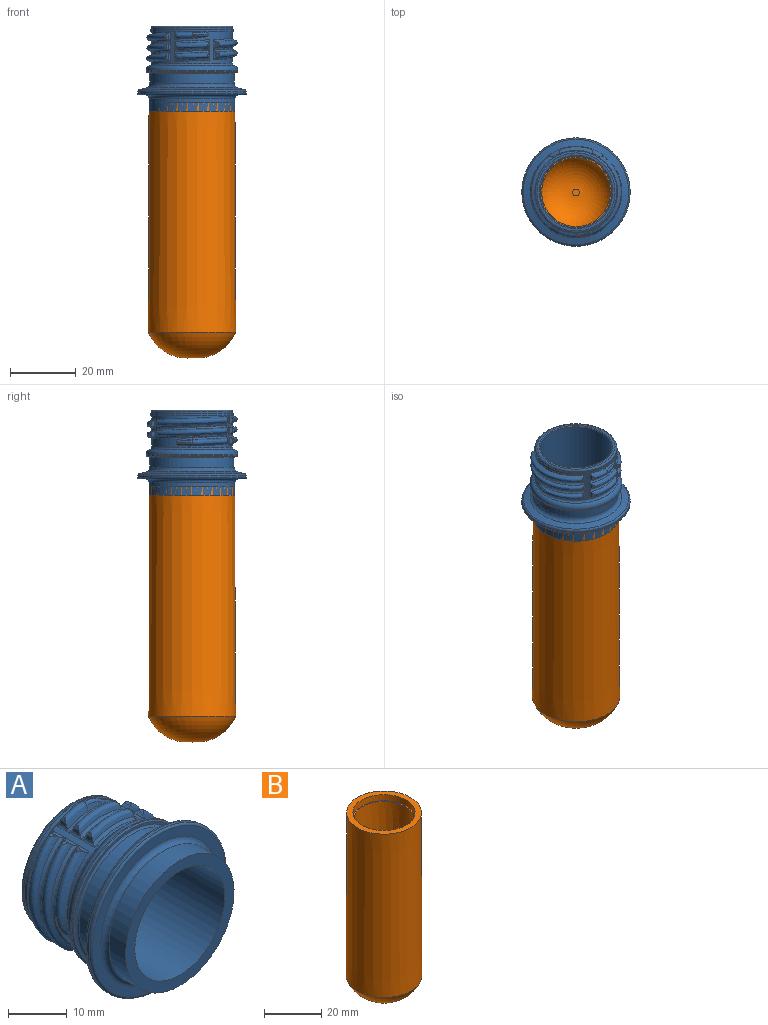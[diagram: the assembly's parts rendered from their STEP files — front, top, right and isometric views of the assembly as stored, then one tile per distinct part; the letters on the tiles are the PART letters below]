
ASSEMBLY  parts=2 mates=1
PART A: 119 faces, bbox 38.3x28.6x38.3 mm
  f0: bspline ~13.4x3.11mm, area 31.2mm2, adj f1,f2,f115,f116,f117,f118
  f1: cylinder r=0.64mm len=1.33mm, axis (0,1,0), area 0mm2, adj f0,f118
  f2: bspline ~12.92x2.26mm, area 8.5mm2, adj f0,f3,f4,f114,f116,f118
  f3: cylinder r=0.58mm len=3mm, axis (0,1,0), area 1.6mm2, adj f2,f4,f116,f117
  f4: cylinder r=12.26mm len=24.51mm, axis (0,-1,0), area 250.7mm2, adj f2,f3,f5,f11,f12,f13,f14,f20
  f5: bspline ~22.44x7.15mm, area 19.3mm2, adj f4,f6,f8,f10,f11,f13
  f6: plane 4.44x3.23mm, normal (-0.53,0,-0.85), area 1.3mm2, adj f5,f7,f8,f11,f12
  f7: cylinder r=0.64mm len=1.34mm, axis (0,1,0), area 0mm2, adj f6,f8
  f8: bspline ~25.39x9.09mm, area 76.1mm2, adj f5,f6,f7,f9,f10,f12
  f9: cylinder r=0.64mm len=1.34mm, axis (0,1,0), area 0mm2, adj f8,f10
  f10: plane 4.44x3.23mm, normal (-0.53,0,0.85), area 1.3mm2, adj f5,f8,f9,f12,f13
  f11: cylinder r=0.58mm len=3mm, axis (0,1,0), area 1.6mm2, adj f4,f5,f6,f12
  f12: bspline ~22.68x7.38mm, area 19.3mm2, adj f4,f6,f8,f10,f11,f13
  f13: cylinder r=0.58mm len=3mm, axis (0,1,0), area 1.6mm2, adj f4,f5,f10,f12
  f14: cylinder r=0.58mm len=3mm, axis (0,1,0), area 1.6mm2, adj f4,f15,f20,f22
  f15: plane 4.44x3.23mm, normal (-0.53,0,-0.85), area 1.3mm2, adj f14,f16,f17,f20,f22
  f16: cylinder r=0.64mm len=1.34mm, axis (0,1,0), area 0mm2, adj f15,f17
  f17: bspline ~25.43x9.14mm, area 75.6mm2, adj f15,f16,f18,f19,f20,f22
  f18: cylinder r=0.64mm len=1.34mm, axis (0,1,0), area 0mm2, adj f17,f19
  f19: plane 4.44x3.23mm, normal (-0.53,0,0.85), area 1.3mm2, adj f17,f18,f20,f21,f22
  f20: bspline ~22.86x7.47mm, area 19.3mm2, adj f4,f14,f15,f17,f19,f21
  f21: cylinder r=0.58mm len=3mm, axis (0,1,0), area 1.6mm2, adj f4,f19,f20,f22
  f22: bspline ~22.44x7.28mm, area 19.3mm2, adj f4,f14,f15,f17,f19,f21
  f23: cylinder r=0.58mm len=2.55mm, axis (0,1,0), area 1.4mm2, adj f4,f24,f26,f30
  f24: plane 4.43x3.23mm, normal (0.53,0,0.85), area 1.3mm2, adj f23,f25,f26,f30
  f25: cylinder r=0.64mm len=1.34mm, axis (0,1,0), area 0mm2, adj f24,f26
  f26: bspline ~25.56x9.31mm, area 87.2mm2, adj f4,f23,f24,f25,f27,f28,f29,f30
  f27: cylinder r=0.64mm len=1.34mm, axis (0,1,0), area 0mm2, adj f26,f28
  f28: plane 4.43x3.23mm, normal (0.53,0,-0.85), area 1.3mm2, adj f26,f27,f29,f30
  f29: cylinder r=0.58mm len=2.55mm, axis (0,1,0), area 1.4mm2, adj f4,f26,f28,f30
  f30: bspline ~22.32x7.13mm, area 19.3mm2, adj f4,f23,f24,f26,f28,f29
  f31: cylinder r=0.58mm len=3mm, axis (0,1,0), area 1.6mm2, adj f4,f32,f37,f39
  f32: plane 4.44x3.34mm, normal (1,0,0), area 1.3mm2, adj f31,f33,f34,f37,f39
  f33: cylinder r=0.64mm len=1.34mm, axis (0,1,0), area 0mm2, adj f32,f34
  f34: bspline ~13.4x2.94mm, area 31.2mm2, adj f32,f33,f35,f36,f37,f39
  f35: cylinder r=0.64mm len=1.34mm, axis (0,1,0), area 0mm2, adj f34,f36
  f36: plane 4.44x3.34mm, normal (-1,0,0), area 1.3mm2, adj f34,f35,f37,f38,f39
  f37: bspline ~12.51x2.13mm, area 8.5mm2, adj f4,f31,f32,f34,f36,f38
  f38: cylinder r=0.58mm len=3mm, axis (0,1,0), area 1.6mm2, adj f4,f36,f37,f39
  f39: bspline ~12.94x2.29mm, area 8.5mm2, adj f4,f31,f32,f34,f36,f38
  f40: torus R=5.71mm, axis (0,1,-0.04), area 4.1mm2, adj f4,f41,f44,f45,f52
  f41: cylinder r=6.35mm len=4.79mm, axis (0,1,-0.04), area 0.8mm2, adj f40,f42,f45,f52
  f42: torus R=5.71mm, axis (0,1,-0.04), area 3.8mm2, adj f41,f43,f45,f51,f52
  f43: cone r=5.93mm half-angle=70deg, axis (0,-1,0.04), area 1.1mm2, adj f42,f45,f50
  f44: cone r=4.89mm half-angle=70deg, axis (0,1,-0.04), area 2.4mm2, adj f4,f40,f45
  f45: bspline ~12.37x8.46mm, area 43.8mm2, adj f4,f40,f41,f42,f43,f44,f46,f47
  f46: cylinder r=0.64mm len=1.34mm, axis (0,1,0), area 0mm2, adj f45,f47
  f47: plane 4.43x3.23mm, normal (0.53,0,0.85), area 1.3mm2, adj f45,f46,f48,f49
  f48: cylinder r=0.58mm len=2.55mm, axis (0,1,0), area 1.4mm2, adj f4,f45,f47,f49
  f49: bspline ~12.82x7.13mm, area 9.7mm2, adj f4,f45,f47,f48,f50
  f50: bspline ~5.36x1.34mm, area 2.7mm2, adj f4,f43,f49,f51
  f51: bspline ~2.32x1.28mm, area 0.9mm2, adj f4,f42,f50,f52
  f52: plane 1.53x0.26mm, normal (0.75,-0.03,-0.66), area 0.2mm2, adj f4,f40,f41,f42,f51
  f53: cylinder r=0.58mm len=3mm, axis (0,1,0), area 1.6mm2, adj f4,f54,f59,f61
  f54: plane 4.44x3.23mm, normal (0.53,0,0.85), area 1.3mm2, adj f53,f55,f56,f59,f61
  f55: cylinder r=0.64mm len=1.34mm, axis (0,1,0), area 0mm2, adj f54,f56
  f56: bspline ~25.41x9.31mm, area 76.2mm2, adj f54,f55,f57,f58,f59,f61
  f57: cylinder r=0.64mm len=1.34mm, axis (0,1,0), area 0mm2, adj f56,f58
  f58: plane 4.44x3.23mm, normal (0.53,0,-0.85), area 1.3mm2, adj f56,f57,f59,f60,f61
  f59: bspline ~22.37x7.08mm, area 19.3mm2, adj f4,f53,f54,f56,f58,f60
  f60: cylinder r=0.58mm len=3mm, axis (0,1,0), area 1.6mm2, adj f4,f58,f59,f61
  f61: bspline ~22.75x7.41mm, area 19.3mm2, adj f4,f53,f54,f56,f58,f60
  f62: cylinder r=0.58mm len=2.1mm, axis (0,1,0), area 1.3mm2, adj f4,f63,f65
  f63: plane 4.42x3.35mm, normal (-1,0,0), area 1.3mm2, adj f62,f64,f65
  f64: cylinder r=0.64mm len=1.34mm, axis (0,1,0), area 0mm2, adj f63,f65
  f65: bspline ~6.85x3.11mm, area 20.6mm2, adj f4,f62,f63,f64,f67,f68,f69,f70
  f66: cylinder r=4.89mm len=0.11mm, axis (0.04,-1,0), area 0mm2, adj f4,f67
  f67: cone r=5.93mm half-angle=70deg, axis (-0.04,1,0), area 3.4mm2, adj f4,f65,f66,f68
  f68: torus R=5.71mm, axis (0.04,-1,0), area 4.2mm2, adj f4,f65,f67,f69
  f69: cylinder r=6.35mm len=5.13mm, axis (0.04,-1,0), area 0.9mm2, adj f4,f65,f68,f70
  f70: torus R=5.71mm, axis (0.04,-1,0), area 4.2mm2, adj f4,f65,f69,f71
  f71: cone r=4.89mm half-angle=70deg, axis (0.04,-1,0), area 3.1mm2, adj f4,f65,f70,f113
  f72: cylinder r=0.58mm len=3mm, axis (0,1,0), area 1.6mm2, adj f4,f73,f110,f112
  f73: plane 4.44x3.34mm, normal (1,0,0), area 1.3mm2, adj f72,f74,f77,f110,f112
  f74: bspline ~13.4x2.94mm, area 31.2mm2, adj f73,f75,f76,f77,f110,f112
  f75: cylinder r=0.64mm len=1.34mm, axis (0,1,0), area 0mm2, adj f74,f76
  f76: plane 4.44x3.34mm, normal (-1,0,0), area 1.3mm2, adj f74,f75,f110,f111,f112
  f77: cylinder r=0.64mm len=1.34mm, axis (0,1,0), area 0mm2, adj f73,f74
  f78: cylinder r=0.58mm len=3mm, axis (0,1,0), area 1.6mm2, adj f4,f79,f107,f109
  f79: plane 4.44x3.34mm, normal (1,0,0), area 1.3mm2, adj f78,f80,f83,f107,f109
  f80: bspline ~13.4x2.94mm, area 31.2mm2, adj f79,f81,f82,f83,f107,f109
  f81: cylinder r=0.64mm len=1.34mm, axis (0,1,0), area 0mm2, adj f80,f82
  f82: plane 4.44x3.34mm, normal (-1,0,0), area 1.3mm2, adj f80,f81,f107,f108,f109
  f83: cylinder r=0.64mm len=1.34mm, axis (0,1,0), area 0mm2, adj f79,f80
  f84: torus R=13.06mm, axis (0,-1,0), area 80.7mm2, adj f4,f85
  f85: torus R=12.38mm, axis (0,-1,0), area 175.8mm2, adj f84,f86
  f86: cylinder r=13.98mm len=27.97mm, axis (0,-1,0), area 22mm2, adj f85,f87
  f87: torus R=13.74mm, axis (0,-1,0), area 34.3mm2, adj f86,f88
  f88: plane 27.47x27.47mm, normal (0,-1,0), area 40.7mm2, adj f87,f89
  f89: torus R=13.25mm, axis (0,-1,0), area 51.3mm2, adj f88,f90
  f90: cylinder r=12.86mm len=25.71mm, axis (0,-1,0), area 232.2mm2, adj f89,f91
  f91: torus R=14.36mm, axis (0,-1,0), area 161.1mm2, adj f90,f92
  f92: cone r=16.04mm half-angle=74deg, axis (0,-1,0), area 205.2mm2, adj f91,f93
  f93: torus R=15.86mm, axis (0,-1,0), area 84.8mm2, adj f92,f94
  f94: cylinder r=16.5mm len=33mm, axis (0,-1,0), area 58.9mm2, adj f93,f95
  f95: torus R=16.1mm, axis (0,-1,0), area 64.6mm2, adj f94,f96
  f96: plane 32.2x32.2mm, normal (0,-1,0), area 190.2mm2, adj f95,f97
  f97: torus R=14.1mm, axis (0,-1,0), area 132.8mm2, adj f96,f98
  f98: cylinder r=13.1mm len=26.19mm, axis (0,-1,0), area 329.1mm2, adj f97,f99
  f99: plane 26.19x26.19mm, normal (0,-1,0), area 167.5mm2, adj f98,f100
  f100: cylinder r=10.87mm len=25.7mm, axis (0,-1,0), area 1755.3mm2, adj f99,f101
  f101: torus R=11.17mm, axis (0,-1,0), area 32.5mm2, adj f100,f102
  f102: plane 23.78x23.78mm, normal (0,1,0), area 52.2mm2, adj f101,f103
  f103: torus R=11.89mm, axis (0,-1,0), area 70.2mm2, adj f102,f104
  f104: cylinder r=12.47mm len=24.94mm, axis (0,-1,0), area 32.9mm2, adj f103,f105
  f105: plane 25.07x25.07mm, normal (0,1,0), area 5.1mm2, adj f104,f106
  f106: cylinder r=12.54mm len=25.07mm, axis (0,-1,0), area 55.1mm2, adj f105,f113
  f107: bspline ~12.87x2.27mm, area 8.5mm2, adj f4,f78,f79,f80,f82,f108
  f108: cylinder r=0.58mm len=3mm, axis (0,1,0), area 1.6mm2, adj f4,f82,f107,f109
  f109: bspline ~12.49x2.32mm, area 8.5mm2, adj f4,f78,f79,f80,f82,f108
  f110: bspline ~12.33x1.98mm, area 8.5mm2, adj f4,f72,f73,f74,f76,f111
  f111: cylinder r=0.58mm len=3mm, axis (0,1,0), area 1.6mm2, adj f4,f76,f110,f112
  f112: bspline ~12x1.89mm, area 8.5mm2, adj f4,f72,f73,f74,f76,f111
  f113: plane 25.09x25.09mm, normal (0,-1,0), area 21.7mm2, adj f4,f71,f106
  f114: cylinder r=0.58mm len=3mm, axis (0,1,0), area 1.6mm2, adj f2,f4,f117,f118
  f115: cylinder r=0.64mm len=1.34mm, axis (0,1,0), area 0mm2, adj f0,f116
  f116: plane 4.44x3.34mm, normal (-1,0,0), area 1.3mm2, adj f0,f2,f3,f115,f117
  f117: bspline ~12.85x2.28mm, area 8.5mm2, adj f0,f3,f4,f114,f116,f118
  f118: plane 4.44x3.34mm, normal (1,0,0), area 1.3mm2, adj f0,f1,f2,f114,f117
PART B: 8 faces, bbox 26.6x26.6x77.7 mm
  f0: torus R=1.55mm, axis (0,0,-1), area 779.7mm2, adj f1
  f1: cone r=13.29mm half-angle=0.2deg, axis (0,0,-1), area 5786.6mm2, adj f0,f2
  f2: plane 26.16x26.16mm, normal (0,0,1), area 166.3mm2, adj f1,f4
  f3: plane 21.74x21.74mm, normal (0,0,1), area 26.7mm2, adj f4,f7
  f4: cylinder r=10.87mm len=21.74mm, axis (0,0,1), area 178.7mm2, adj f2,f3
  f5: torus R=1.55mm, axis (0,0,-1), area 481.5mm2, adj f6,f7
  f6: plane 2.04x2.04mm, normal (0,0,1), area 3.3mm2, adj f5
  f7: cone r=10.67mm half-angle=0.2deg, axis (0,0,-1), area 4429.6mm2, adj f3,f5
PLACE A rot(axis=(1,0,0),90deg) t=(-23.72,11.31,99.73)mm
PLACE B t=(-23.72,11.31,-1.26)mm
MATE fastened A.f4 <-> B.f0  axis (0,0,-1) through (-23.72,11.31,73.73)mm
